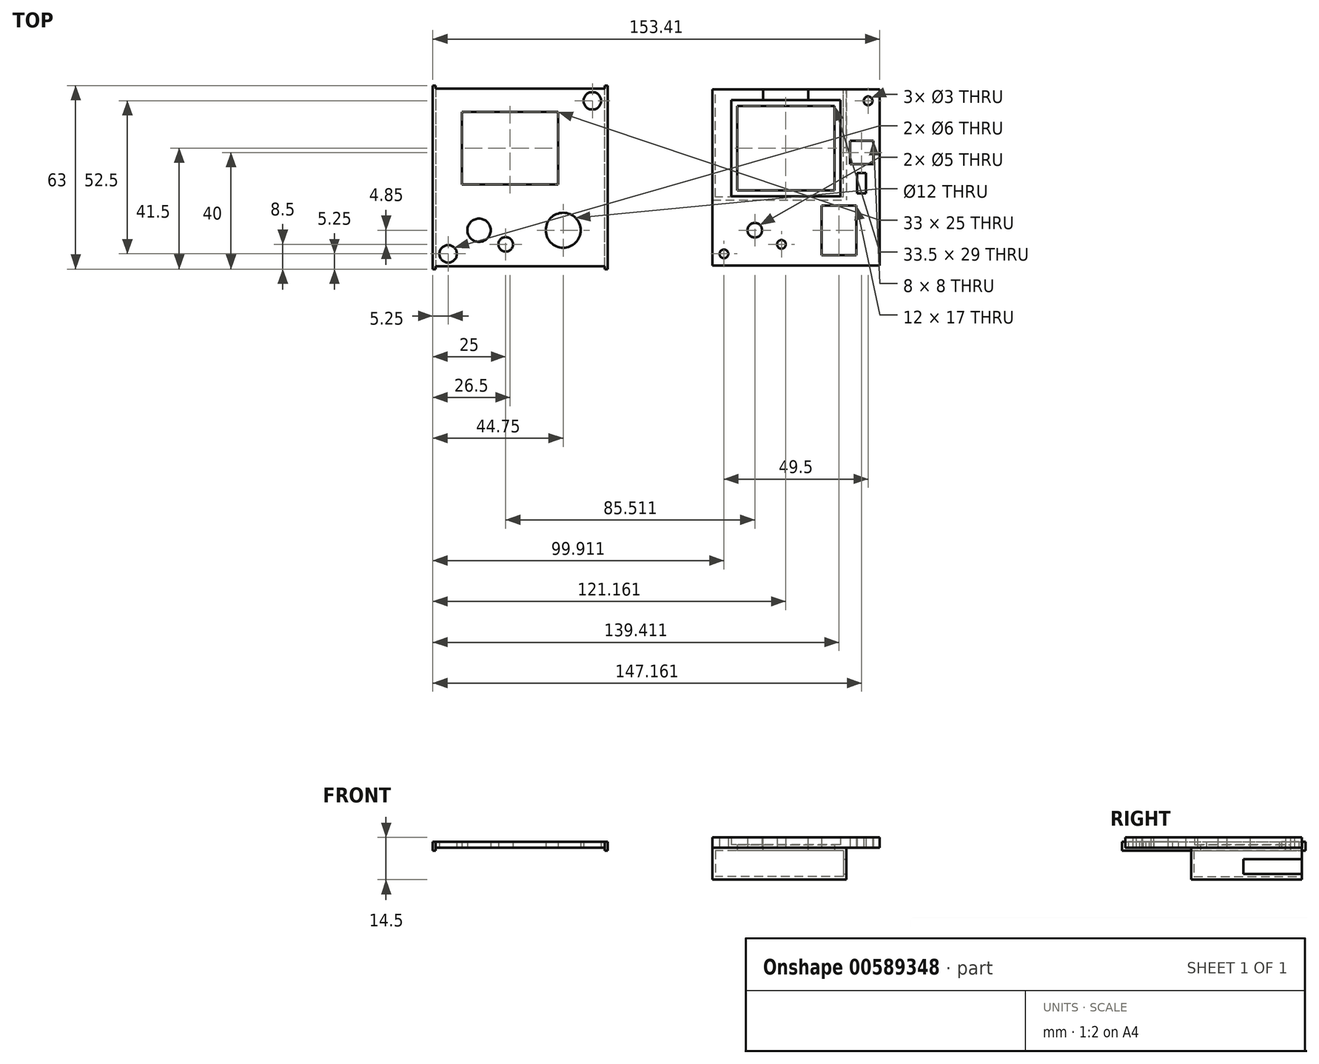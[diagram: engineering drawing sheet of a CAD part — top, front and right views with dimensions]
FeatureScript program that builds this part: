
annotation { "Feature Type Name" : "Feature", "Feature Type Description" : "" }
export const myFeature = defineFeature(function(context is Context, id is Id, definition is map)
    precondition{}
    {
        {
            var Q0;
            Q0=qCreatedBy(makeId("Top.planeOp"),FACE);
            var sketch = newSketch(context, id + "F0", { "sketchPlane" : qUnion([Q0])});
            skLineSegment(sketch, "E0.bottom", {"start": v(29, -30.5) * mm, "end": v(-29, -30.5) * mm});
            skLineSegment(sketch, "E0.top", {"start": v(29, 30.5) * mm, "end": v(-29, 30.5) * mm});
            skLineSegment(sketch, "E0.left", {"start": v(29, -30.5) * mm, "end": v(29, 30.5) * mm});
            skLineSegment(sketch, "E0.right", {"start": v(-29, -30.5) * mm, "end": v(-29, 30.5) * mm});
            skPoint(sketch, "E0.middle", {"position": v(0, 0) * mm});
            skLineSegment(sketch, "E1.bottom", {"start": v(13, -2.5) * mm, "end": v(-20, -2.5) * mm});
            skLineSegment(sketch, "E1.top", {"start": v(13, 22.5) * mm, "end": v(-20, 22.5) * mm});
            skLineSegment(sketch, "E1.left", {"start": v(13, -2.5) * mm, "end": v(13, 22.5) * mm});
            skLineSegment(sketch, "E1.right", {"start": v(-20, -2.5) * mm, "end": v(-20, 22.5) * mm});
            skLineSegment(sketch, "E2.bottom", {"start": v(-29, 30.5) * mm, "end": v(29, 30.5) * mm});
            skLineSegment(sketch, "E2.top", {"start": v(-29, 31.5) * mm, "end": v(29, 31.5) * mm});
            skLineSegment(sketch, "E2.left", {"start": v(-29, 30.5) * mm, "end": v(-29, 31.5) * mm});
            skLineSegment(sketch, "E2.right", {"start": v(29, 30.5) * mm, "end": v(29, 31.5) * mm});
            skLineSegment(sketch, "E3.bottom", {"start": v(-29, -30.5) * mm, "end": v(29, -30.5) * mm});
            skLineSegment(sketch, "E3.top", {"start": v(-29, -31.5) * mm, "end": v(29, -31.5) * mm});
            skLineSegment(sketch, "E3.left", {"start": v(-29, -30.5) * mm, "end": v(-29, -31.5) * mm});
            skLineSegment(sketch, "E3.right", {"start": v(29, -30.5) * mm, "end": v(29, -31.5) * mm});
            skLineSegment(sketch, "E4.bottom", {"start": v(-29, -31.5) * mm, "end": v(-30, -31.5) * mm});
            skLineSegment(sketch, "E4.top", {"start": v(-29, 31.5) * mm, "end": v(-30, 31.5) * mm});
            skLineSegment(sketch, "E4.left", {"start": v(-29, -31.5) * mm, "end": v(-29, 31.5) * mm});
            skLineSegment(sketch, "E4.right", {"start": v(-30, -31.5) * mm, "end": v(-30, 31.5) * mm});
            skLineSegment(sketch, "E5.bottom", {"start": v(29, -31.5) * mm, "end": v(30, -31.5) * mm});
            skLineSegment(sketch, "E5.top", {"start": v(29, 31.5) * mm, "end": v(30, 31.5) * mm});
            skLineSegment(sketch, "E5.left", {"start": v(29, -31.5) * mm, "end": v(29, 31.5) * mm});
            skLineSegment(sketch, "E5.right", {"start": v(30, -31.5) * mm, "end": v(30, 31.5) * mm});
            skCircle(sketch, "E6", {"center": v(14.75, -18.15) * mm, "radius": 6 * mm});
            skCircle(sketch, "E7", {"center": v(-14.15, -18.15) * mm, "radius": 4 * mm});
            skCircle(sketch, "E8", {"center": v(-5, -23) * mm, "radius": 2.5 * mm});
            skPoint(sketch, "E9", {"position": v(-3.5, 10) * mm});
            skPoint(sketch, "E9.positionSnap0", {"position": v(-3.5, 22.5) * mm});
            skPoint(sketch, "E9.positionSnap1", {"position": v(-20, 10) * mm});
            skCircle(sketch, "E10", {"center": v(-24.75, -26.25) * mm, "radius": 3 * mm});
            skCircle(sketch, "E11", {"center": v(24.75, 26.25) * mm, "radius": 3 * mm});
            skSolve(sketch);
        }
        {
            var Q0;
            Q0=qCreatedBy(makeId("Top.planeOp"),FACE);
            var sketch = newSketch(context, id + "F1", { "sketchPlane" : qUnion([Q0])});
            skLineSegment(sketch, "E12.bottom", {"start": v(123.41, -30.25) * mm, "end": v(65.91, -30.25) * mm});
            skLineSegment(sketch, "E12.top", {"start": v(123.41, 30.25) * mm, "end": v(65.91, 30.25) * mm});
            skLineSegment(sketch, "E12.left", {"start": v(123.41, -30.25) * mm, "end": v(123.41, 30.25) * mm});
            skLineSegment(sketch, "E12.right", {"start": v(65.91, -30.25) * mm, "end": v(65.91, 30.25) * mm});
            skPoint(sketch, "E12.middle", {"position": v(94.66, 0) * mm});
            skLineSegment(sketch, "E13.bottom", {"start": v(109.91, -6.5) * mm, "end": v(72.41, -6.5) * mm});
            skLineSegment(sketch, "E13.top", {"start": v(109.91, 26.5) * mm, "end": v(72.41, 26.5) * mm});
            skLineSegment(sketch, "E13.left", {"start": v(109.91, -6.5) * mm, "end": v(109.91, 26.5) * mm});
            skLineSegment(sketch, "E13.right", {"start": v(72.41, -6.5) * mm, "end": v(72.41, 26.5) * mm});
            skCircle(sketch, "E14", {"center": v(69.91, -26.25) * mm, "radius": 1.5 * mm});
            skCircle(sketch, "E15", {"center": v(119.41, 26.25) * mm, "radius": 1.5 * mm});
            skCircle(sketch, "E16", {"center": v(109.41, -18.15) * mm, "radius": 6.1 * mm, "construction": true});
            skLineSegment(sketch, "E17.bottom", {"start": v(115.66, 1.5) * mm, "end": v(118.66, 1.5) * mm});
            skLineSegment(sketch, "E17.top", {"start": v(115.66, -5.5) * mm, "end": v(118.66, -5.5) * mm});
            skLineSegment(sketch, "E17.left", {"start": v(115.66, 1.5) * mm, "end": v(115.66, -5.5) * mm});
            skLineSegment(sketch, "E17.right", {"start": v(118.66, 1.5) * mm, "end": v(118.66, -5.5) * mm});
            skPoint(sketch, "E18.centerSnap0", {"position": v(117.16, 1.5) * mm});
            skCircle(sketch, "E19", {"center": v(80.51, -18.15) * mm, "radius": 2.5 * mm});
            skCircle(sketch, "E20", {"center": v(89.66, -23) * mm, "radius": 1.5 * mm});
            skLineSegment(sketch, "E21.bottom", {"start": v(115.41, -26.65) * mm, "end": v(103.41, -26.65) * mm});
            skLineSegment(sketch, "E21.top", {"start": v(115.41, -9.65) * mm, "end": v(103.41, -9.65) * mm});
            skLineSegment(sketch, "E21.left", {"start": v(115.41, -26.65) * mm, "end": v(115.41, -9.65) * mm});
            skLineSegment(sketch, "E21.right", {"start": v(103.41, -26.65) * mm, "end": v(103.41, -9.65) * mm});
            skLineSegment(sketch, "E22.bottom", {"start": v(119.66, 6) * mm, "end": v(114.66, 6) * mm, "construction": true});
            skLineSegment(sketch, "E22.top", {"start": v(119.66, 11) * mm, "end": v(114.66, 11) * mm, "construction": true});
            skLineSegment(sketch, "E22.left", {"start": v(119.66, 6) * mm, "end": v(119.66, 11) * mm, "construction": true});
            skLineSegment(sketch, "E22.right", {"start": v(114.66, 6) * mm, "end": v(114.66, 11) * mm, "construction": true});
            skPoint(sketch, "E22.middle", {"position": v(117.16, 8.5) * mm});
            skPoint(sketch, "E23", {"position": v(91.16, 10) * mm});
            skPoint(sketch, "E23.positionSnap0", {"position": v(91.16, 26.5) * mm});
            skPoint(sketch, "E23.positionSnap1", {"position": v(72.41, 10) * mm});
            skLineSegment(sketch, "E24.bottom", {"start": v(121.16, 4.5) * mm, "end": v(113.16, 4.5) * mm});
            skLineSegment(sketch, "E24.top", {"start": v(121.16, 12.5) * mm, "end": v(113.16, 12.5) * mm});
            skLineSegment(sketch, "E24.left", {"start": v(121.16, 4.5) * mm, "end": v(121.16, 12.5) * mm});
            skLineSegment(sketch, "E24.right", {"start": v(113.16, 4.5) * mm, "end": v(113.16, 12.5) * mm});
            skCircle(sketch, "E25", {"center": v(69.91, -26.25) * mm, "radius": 3 * mm, "construction": true});
            skCircle(sketch, "E26", {"center": v(119.41, 26.25) * mm, "radius": 3 * mm, "construction": true});
            skSolve(sketch);
        }
        {
            var Q0;
            Q0=makeQuery(id+"F1.imprint","IMPRINT",FACE,{"disambiguationData":[TD([[makeQuery(id+"F1.imprint","IMPRINT",EDGE,{"derivedFrom":sQuery(id+"F1.wireOp",EDGE,"E12.bottom")}),-1.0]])]});
            extrude(context, id + "F2", {"entities" : qUnion([Q0]), "depth" : 3.5 * mm});
        }
        {
            var Q0;
            Q0=makeQuery(id+"F2.opExtrude","CAP_FACE",FACE,{"disambiguationData":[OSD([sQuery(id+"F1.wireOp",EDGE,"E12.bottom"),sQuery(id+"F1.wireOp",EDGE,"E12.top"),sQuery(id+"F1.wireOp",EDGE,"E12.left"),sQuery(id+"F1.wireOp",EDGE,"E12.right"),sQuery(id+"F1.wireOp",EDGE,"E13.bottom"),sQuery(id+"F1.wireOp",EDGE,"E13.top"),sQuery(id+"F1.wireOp",EDGE,"E13.left"),sQuery(id+"F1.wireOp",EDGE,"E13.right"),sQuery(id+"F1.wireOp",EDGE,"E14"),sQuery(id+"F1.wireOp",EDGE,"E15"),sQuery(id+"F1.wireOp",EDGE,"E16"),sQuery(id+"F1.wireOp",EDGE,"E17.bottom"),sQuery(id+"F1.wireOp",EDGE,"E17.top"),sQuery(id+"F1.wireOp",EDGE,"E17.left"),sQuery(id+"F1.wireOp",EDGE,"E17.right"),sQuery(id+"F1.wireOp",EDGE,"E18"),sQuery(id+"F1.wireOp",EDGE,"E19"),sQuery(id+"F1.wireOp",EDGE,"E20")])],"isStart":false});
            var sketch = newSketch(context, id + "F3", { "sketchPlane" : qUnion([Q0])});
            skLineSegment(sketch, "E27.bottom", {"start": v(98.91, 26.5) * mm, "end": v(83.41, 26.5) * mm});
            skLineSegment(sketch, "E27.top", {"start": v(98.91, 30.25) * mm, "end": v(83.41, 30.25) * mm});
            skLineSegment(sketch, "E27.left", {"start": v(98.91, 26.5) * mm, "end": v(98.91, 30.25) * mm});
            skLineSegment(sketch, "E27.right", {"start": v(83.41, 26.5) * mm, "end": v(83.41, 30.25) * mm});
            skPoint(sketch, "E27.middle", {"position": v(91.16, 28.38) * mm});
            skPoint(sketch, "E27.middle.positionSnap0", {"position": v(91.16, 26.5) * mm});
            skPoint(sketch, "E27.centerSnap0", {"position": v(91.16, 26.5) * mm});
            skSolve(sketch);
        }
        {
            var Q0;
            Q0=makeQuery(id+"F2.opExtrude","CAP_FACE",FACE,{"disambiguationData":[OSD([sQuery(id+"F1.wireOp",EDGE,"E12.bottom"),sQuery(id+"F1.wireOp",EDGE,"E12.top"),sQuery(id+"F1.wireOp",EDGE,"E12.left"),sQuery(id+"F1.wireOp",EDGE,"E12.right"),sQuery(id+"F1.wireOp",EDGE,"E13.bottom"),sQuery(id+"F1.wireOp",EDGE,"E13.top"),sQuery(id+"F1.wireOp",EDGE,"E13.left"),sQuery(id+"F1.wireOp",EDGE,"E13.right"),sQuery(id+"F1.wireOp",EDGE,"E14"),sQuery(id+"F1.wireOp",EDGE,"E15"),sQuery(id+"F1.wireOp",EDGE,"E16"),sQuery(id+"F1.wireOp",EDGE,"E17.bottom"),sQuery(id+"F1.wireOp",EDGE,"E17.top"),sQuery(id+"F1.wireOp",EDGE,"E17.left"),sQuery(id+"F1.wireOp",EDGE,"E17.right"),sQuery(id+"F1.wireOp",EDGE,"E18"),sQuery(id+"F1.wireOp",EDGE,"E19"),sQuery(id+"F1.wireOp",EDGE,"E20")])],"isStart":true});
            var sketch = newSketch(context, id + "F4", { "sketchPlane" : qUnion([Q0])});
            skLineSegment(sketch, "E28.bottom", {"start": v(72.41, -26.5) * mm, "end": v(109.91, -26.5) * mm});
            skLineSegment(sketch, "E28.top", {"start": v(72.41, 6.5) * mm, "end": v(109.91, 6.5) * mm});
            skLineSegment(sketch, "E28.left", {"start": v(72.41, -26.5) * mm, "end": v(72.41, 6.5) * mm});
            skLineSegment(sketch, "E28.right", {"start": v(109.91, -26.5) * mm, "end": v(109.91, 6.5) * mm});
            skLineSegment(sketch, "E29.0", {"start": v(107.91, -24.5) * mm, "end": v(107.91, 4.5) * mm});
            skLineSegment(sketch, "E29.1", {"start": v(74.41, -24.5) * mm, "end": v(107.91, -24.5) * mm});
            skLineSegment(sketch, "E29.2", {"start": v(74.41, -24.5) * mm, "end": v(74.41, 4.5) * mm});
            skLineSegment(sketch, "E29.3", {"start": v(74.41, 4.5) * mm, "end": v(107.91, 4.5) * mm});
            skSolve(sketch);
        }
        {
            var Q0;
            Q0=makeQuery(id+"F4.imprint","IMPRINT",FACE,{"disambiguationData":[TD([[makeQuery(id+"F4.imprint","IMPRINT",EDGE,{"derivedFrom":sQuery(id+"F4.wireOp",EDGE,"E28.bottom")}),-1.0]])]});
            extrude(context, id + "F5", {"entities" : qUnion([Q0]), "operationType" : NewBodyOperationType.ADD, "oppositeDirection" : true, "depth" : 1 * mm});
        }
        {
            var Q0;
            Q0=makeQuery(id+"F3.imprint","IMPRINT",FACE,{"disambiguationData":[TD([[makeQuery(id+"F3.imprint","IMPRINT",EDGE,{"derivedFrom":sQuery(id+"F3.wireOp",EDGE,"E27.bottom")}),-1.0]])]});
            extrude(context, id + "F6", {"entities" : qUnion([Q0]), "operationType" : NewBodyOperationType.REMOVE, "oppositeDirection" : true, "depth" : 2.5 * mm});
        }
        {
            var Q0;
            Q0=makeQuery(id+"F5.boolean.opBoolean","MERGE",FACE,{"derivedFrom":[makeQuery(id+"F2.opExtrude","CAP_FACE",FACE,{"disambiguationData":[OSD([sQuery(id+"F1.wireOp",EDGE,"E12.bottom"),sQuery(id+"F1.wireOp",EDGE,"E12.top"),sQuery(id+"F1.wireOp",EDGE,"E12.left"),sQuery(id+"F1.wireOp",EDGE,"E12.right"),sQuery(id+"F1.wireOp",EDGE,"E13.bottom"),sQuery(id+"F1.wireOp",EDGE,"E13.top"),sQuery(id+"F1.wireOp",EDGE,"E13.left"),sQuery(id+"F1.wireOp",EDGE,"E13.right"),sQuery(id+"F1.wireOp",EDGE,"E14"),sQuery(id+"F1.wireOp",EDGE,"E15"),sQuery(id+"F1.wireOp",EDGE,"E16"),sQuery(id+"F1.wireOp",EDGE,"E17.bottom"),sQuery(id+"F1.wireOp",EDGE,"E17.top"),sQuery(id+"F1.wireOp",EDGE,"E17.left"),sQuery(id+"F1.wireOp",EDGE,"E17.right"),sQuery(id+"F1.wireOp",EDGE,"E18"),sQuery(id+"F1.wireOp",EDGE,"E19"),sQuery(id+"F1.wireOp",EDGE,"E20")])],"isStart":true}),makeQuery(id+"F5.opExtrude","CAP_FACE",FACE,{"disambiguationData":[OSD([sQuery(id+"F4.wireOp",EDGE,"E28.bottom"),sQuery(id+"F4.wireOp",EDGE,"E28.top"),sQuery(id+"F4.wireOp",EDGE,"E28.left"),sQuery(id+"F4.wireOp",EDGE,"E28.right"),sQuery(id+"F4.wireOp",EDGE,"E29.0"),sQuery(id+"F4.wireOp",EDGE,"E29.1"),sQuery(id+"F4.wireOp",EDGE,"E29.2"),sQuery(id+"F4.wireOp",EDGE,"E29.3")])],"isStart":true})]});
            var sketch = newSketch(context, id + "F7", { "sketchPlane" : qUnion([Q0])});
            skLineSegment(sketch, "E30.bottom", {"start": v(118.16, -30.25) * mm, "end": v(71.16, -30.25) * mm, "construction": true});
            skLineSegment(sketch, "E30.top", {"start": v(118.16, 1.75) * mm, "end": v(71.16, 1.75) * mm, "construction": true});
            skLineSegment(sketch, "E30.left", {"start": v(118.16, -30.25) * mm, "end": v(118.16, 1.75) * mm, "construction": true});
            skLineSegment(sketch, "E30.right", {"start": v(71.16, -30.25) * mm, "end": v(71.16, 1.75) * mm, "construction": true});
            skSolve(sketch);
        }
        {
            var Q0;
            Q0=makeQuery(id+"F0.imprint","IMPRINT",FACE,{"disambiguationData":[TD([[makeQuery(id+"F0.imprint","IMPRINT",EDGE,{"derivedFrom":sQuery(id+"F0.wireOp",EDGE,"E1.bottom")}),1.0]])]});
            var Q1;
            {var subQ3=sQuery(id+"F0.wireOp",EDGE,"E4.bottom");Q1=makeQuery(id+"F0.imprint","IMPRINT",FACE,{"disambiguationData":[TD([[makeQuery(id+"F0.imprint","IMPRINT",EDGE,{"derivedFrom":subQ3}),-1.0]])]});}
            var Q2;
            {var subQ0=sQuery(id+"F0.wireOp",EDGE,"E2.bottom");Q2=makeQuery(id+"F0.imprint","IMPRINT",FACE,{"disambiguationData":[TD([[makeQuery(id+"F0.imprint","IMPRINT",EDGE,{"derivedFrom":subQ0}),1.0]])]});}
            var Q3;
            {var subQ3=sQuery(id+"F0.wireOp",EDGE,"E5.bottom");Q3=makeQuery(id+"F0.imprint","IMPRINT",FACE,{"disambiguationData":[TD([[makeQuery(id+"F0.imprint","IMPRINT",EDGE,{"derivedFrom":subQ3}),1.0]])]});}
            var Q4;
            {var subQ0=sQuery(id+"F0.wireOp",EDGE,"E3.bottom");Q4=makeQuery(id+"F0.imprint","IMPRINT",FACE,{"disambiguationData":[TD([[makeQuery(id+"F0.imprint","IMPRINT",EDGE,{"derivedFrom":subQ0}),-1.0]])]});}
            extrude(context, id + "F8", {"entities" : qUnion([Q0, Q1, Q2, Q3, Q4]), "depth" : 2 * mm});
        }
        {
            var Q0;
            {var subQ0=sQuery(id+"F0.wireOp",EDGE,"E2.bottom");Q0=makeQuery(id+"F0.imprint","IMPRINT",FACE,{"disambiguationData":[TD([[makeQuery(id+"F0.imprint","IMPRINT",EDGE,{"derivedFrom":subQ0}),1.0]])]});}
            var Q1;
            {var subQ3=sQuery(id+"F0.wireOp",EDGE,"E4.bottom");Q1=makeQuery(id+"F0.imprint","IMPRINT",FACE,{"disambiguationData":[TD([[makeQuery(id+"F0.imprint","IMPRINT",EDGE,{"derivedFrom":subQ3}),-1.0]])]});}
            var Q2;
            {var subQ0=sQuery(id+"F0.wireOp",EDGE,"E3.bottom");Q2=makeQuery(id+"F0.imprint","IMPRINT",FACE,{"disambiguationData":[TD([[makeQuery(id+"F0.imprint","IMPRINT",EDGE,{"derivedFrom":subQ0}),-1.0]])]});}
            var Q3;
            {var subQ3=sQuery(id+"F0.wireOp",EDGE,"E5.bottom");Q3=makeQuery(id+"F0.imprint","IMPRINT",FACE,{"disambiguationData":[TD([[makeQuery(id+"F0.imprint","IMPRINT",EDGE,{"derivedFrom":subQ3}),1.0]])]});}
            extrude(context, id + "F9", {"entities" : qUnion([Q0, Q1, Q2, Q3]), "operationType" : NewBodyOperationType.ADD, "oppositeDirection" : true, "depth" : 1 * mm});
        }
        {
            var Q0;
            Q0=makeQuery(id+"F8.opExtrude","CAP_FACE",FACE,{"disambiguationData":[OSD([sQuery(id+"F0.wireOp",EDGE,"E1.bottom"),sQuery(id+"F0.wireOp",EDGE,"E1.top"),sQuery(id+"F0.wireOp",EDGE,"E1.left"),sQuery(id+"F0.wireOp",EDGE,"E1.right"),sQuery(id+"F0.wireOp",EDGE,"E2.top"),sQuery(id+"F0.wireOp",EDGE,"E3.top"),sQuery(id+"F0.wireOp",EDGE,"E4.bottom"),sQuery(id+"F0.wireOp",EDGE,"E4.top"),sQuery(id+"F0.wireOp",EDGE,"E4.right"),sQuery(id+"F0.wireOp",EDGE,"E5.bottom"),sQuery(id+"F0.wireOp",EDGE,"E5.top"),sQuery(id+"F0.wireOp",EDGE,"E5.right"),sQuery(id+"F0.wireOp",EDGE,"E6"),sQuery(id+"F0.wireOp",EDGE,"E7"),sQuery(id+"F0.wireOp",EDGE,"E8")])],"isStart":false});
            var sketch = newSketch(context, id + "F10", { "sketchPlane" : qUnion([Q0])});
            skLineSegment(sketch, "E31.bottom", {"start": v(-20, 22.5) * mm, "end": v(13, 22.5) * mm});
            skLineSegment(sketch, "E31.top", {"start": v(-20, 23.5) * mm, "end": v(13, 23.5) * mm});
            skLineSegment(sketch, "E31.left", {"start": v(-20, 22.5) * mm, "end": v(-20, 23.5) * mm});
            skLineSegment(sketch, "E31.right", {"start": v(13, 22.5) * mm, "end": v(13, 23.5) * mm});
            skLineSegment(sketch, "E32.bottom", {"start": v(-20, 23.5) * mm, "end": v(-21, 23.5) * mm});
            skLineSegment(sketch, "E32.top", {"start": v(-20, -2.5) * mm, "end": v(-21, -2.5) * mm});
            skLineSegment(sketch, "E32.left", {"start": v(-20, 23.5) * mm, "end": v(-20, -2.5) * mm});
            skLineSegment(sketch, "E32.right", {"start": v(-21, 23.5) * mm, "end": v(-21, -2.5) * mm});
            skLineSegment(sketch, "E33.bottom", {"start": v(13, 23.5) * mm, "end": v(14, 23.5) * mm});
            skLineSegment(sketch, "E33.top", {"start": v(13, -2.5) * mm, "end": v(14, -2.5) * mm});
            skLineSegment(sketch, "E33.left", {"start": v(13, 23.5) * mm, "end": v(13, -2.5) * mm});
            skLineSegment(sketch, "E33.right", {"start": v(14, 23.5) * mm, "end": v(14, -2.5) * mm});
            skLineSegment(sketch, "E34.bottom", {"start": v(-21, -2.5) * mm, "end": v(14, -2.5) * mm});
            skLineSegment(sketch, "E34.top", {"start": v(-21, -3.5) * mm, "end": v(14, -3.5) * mm});
            skLineSegment(sketch, "E34.left", {"start": v(-21, -2.5) * mm, "end": v(-21, -3.5) * mm});
            skLineSegment(sketch, "E34.right", {"start": v(14, -2.5) * mm, "end": v(14, -3.5) * mm});
            skSolve(sketch);
        }
        {
            var Q0;
            Q0=makeQuery(id+"F7.imprint","IMPRINT",FACE,{"disambiguationData":[TD([[makeQuery(id+"F7.imprint","IMPRINT",EDGE,{"derivedFrom":makeQuery(id+"F2.opExtrude","CAP_EDGE",EDGE,{"disambiguationData":[OSD([sQuery(id+"F1.wireOp",EDGE,"E12.bottom")])],"isStart":true})}),1.0]])]});
            var sketch = newSketch(context, id + "F11", { "sketchPlane" : qUnion([Q0])});
            skPoint(sketch, "E35.0", {"position": v(65.91, -30.25) * mm});
            skPoint(sketch, "E36.0", {"position": v(123.41, -30.25) * mm});
            skLineSegment(sketch, "E37.bottom", {"start": v(65.91, -30.25) * mm, "end": v(111.91, -30.25) * mm});
            skLineSegment(sketch, "E37.top", {"start": v(65.91, 7.75) * mm, "end": v(111.91, 7.75) * mm});
            skLineSegment(sketch, "E37.left", {"start": v(65.91, -30.25) * mm, "end": v(65.91, 7.75) * mm});
            skLineSegment(sketch, "E37.right", {"start": v(111.91, -30.25) * mm, "end": v(111.91, 7.75) * mm});
            skSolve(sketch);
        }
        {
            var Q0;
            Q0=qSketchRegion(id+"F11",true);
            extrude(context, id + "F12", {"entities" : qUnion([Q0]), "operationType" : NewBodyOperationType.ADD, "depth" : 11 * mm});
        }
        {
            var Q0;
            Q0=makeQuery(id+"F12.boolean.opBoolean","MERGE",FACE,{"derivedFrom":[makeQuery(id+"F2.opExtrude","SWEPT_FACE",FACE,{"disambiguationData":[OSD([sQuery(id+"F1.wireOp",EDGE,"E12.top")])]}),makeQuery(id+"F12.opExtrude","SWEPT_FACE",FACE,{"disambiguationData":[OSD([sQuery(id+"F11.wireOp",EDGE,"E37.bottom")])]})]});
            var sketch = newSketch(context, id + "F13", { "sketchPlane" : qUnion([Q0])});
            skLineSegment(sketch, "E38.bottom", {"start": v(-110.91, -1) * mm, "end": v(-66.91, -1) * mm});
            skLineSegment(sketch, "E38.top", {"start": v(-110.91, -10) * mm, "end": v(-66.91, -10) * mm});
            skLineSegment(sketch, "E38.left", {"start": v(-110.91, -1) * mm, "end": v(-110.91, -10) * mm});
            skLineSegment(sketch, "E38.right", {"start": v(-66.91, -1) * mm, "end": v(-66.91, -10) * mm});
            skSolve(sketch);
        }
        {
            var Q0;
            Q0=qSketchRegion(id+"F13",true);
            extrude(context, id + "F14", {"entities" : qUnion([Q0]), "operationType" : NewBodyOperationType.REMOVE, "oppositeDirection" : true, "depth" : 37 * mm});
        }
        {
            var Q0;
            Q0=makeQuery(id+"F12.boolean.opBoolean","MERGE",FACE,{"derivedFrom":[makeQuery(id+"F2.opExtrude","SWEPT_FACE",FACE,{"disambiguationData":[OSD([sQuery(id+"F1.wireOp",EDGE,"E12.top")])]}),makeQuery(id+"F12.opExtrude","SWEPT_FACE",FACE,{"disambiguationData":[OSD([sQuery(id+"F11.wireOp",EDGE,"E37.bottom")])]})]});
            var sketch = newSketch(context, id + "F15", { "sketchPlane" : qUnion([Q0])});
            skLineSegment(sketch, "E39.bottom", {"start": v(-110.91, -9) * mm, "end": v(-111.91, -9) * mm});
            skLineSegment(sketch, "E39.top", {"start": v(-110.91, -4) * mm, "end": v(-111.91, -4) * mm});
            skLineSegment(sketch, "E39.left", {"start": v(-110.91, -9) * mm, "end": v(-110.91, -4) * mm});
            skLineSegment(sketch, "E39.right", {"start": v(-111.91, -9) * mm, "end": v(-111.91, -4) * mm});
            skSolve(sketch);
        }
        {
            var Q0;
            Q0=qSketchRegion(id+"F15",true);
            extrude(context, id + "F16", {"entities" : qUnion([Q0]), "operationType" : NewBodyOperationType.REMOVE, "oppositeDirection" : true, "depth" : 20 * mm});
        }
        {
            var Q0;
            Q0=makeQuery(id+"F6.boolean.opBoolean","MERGE",FACE,{"derivedFrom":[makeQuery(id+"F5.opExtrude","CAP_FACE",FACE,{"disambiguationData":[OSD([sQuery(id+"F4.wireOp",EDGE,"E28.bottom"),sQuery(id+"F4.wireOp",EDGE,"E28.top"),sQuery(id+"F4.wireOp",EDGE,"E28.left"),sQuery(id+"F4.wireOp",EDGE,"E28.right"),sQuery(id+"F4.wireOp",EDGE,"E29.0"),sQuery(id+"F4.wireOp",EDGE,"E29.1"),sQuery(id+"F4.wireOp",EDGE,"E29.2"),sQuery(id+"F4.wireOp",EDGE,"E29.3")])],"isStart":false}),makeQuery(id+"F6.opExtrude","CAP_FACE",FACE,{"disambiguationData":[OSD([sQuery(id+"F3.wireOp",EDGE,"E27.bottom"),sQuery(id+"F3.wireOp",EDGE,"E27.top"),sQuery(id+"F3.wireOp",EDGE,"E27.left"),sQuery(id+"F3.wireOp",EDGE,"E27.right")])],"isStart":false})]});
            var sketch = newSketch(context, id + "F17", { "sketchPlane" : qUnion([Q0])});
            skPoint(sketch, "E40.0", {"position": v(74.41, 24.5) * mm});
            skPoint(sketch, "E40.1", {"position": v(107.91, -4.5) * mm});
            skLineSegment(sketch, "E41.bottom", {"start": v(74.41, 24.5) * mm, "end": v(107.91, 24.5) * mm});
            skLineSegment(sketch, "E41.top", {"start": v(74.41, -4.5) * mm, "end": v(107.91, -4.5) * mm});
            skLineSegment(sketch, "E41.left", {"start": v(74.41, -4.5) * mm, "end": v(74.41, 24.5) * mm});
            skLineSegment(sketch, "E41.right", {"start": v(107.91, -4.5) * mm, "end": v(107.91, 24.5) * mm});
            skLineSegment(sketch, "E42.bottom", {"start": v(83.41, 30.25) * mm, "end": v(98.91, 30.25) * mm});
            skLineSegment(sketch, "E42.top", {"start": v(83.41, 26.5) * mm, "end": v(98.91, 26.5) * mm});
            skLineSegment(sketch, "E42.left", {"start": v(83.41, 30.25) * mm, "end": v(83.41, 26.5) * mm});
            skLineSegment(sketch, "E42.right", {"start": v(98.91, 30.25) * mm, "end": v(98.91, 26.5) * mm});
            skSolve(sketch);
        }
        {
            var Q0;
            Q0=qSketchRegion(id+"F17",true);
            extrude(context, id + "F18", {"entities" : qUnion([Q0]), "operationType" : NewBodyOperationType.REMOVE, "oppositeDirection" : true, "depth" : 4 * mm});
        }
    });
